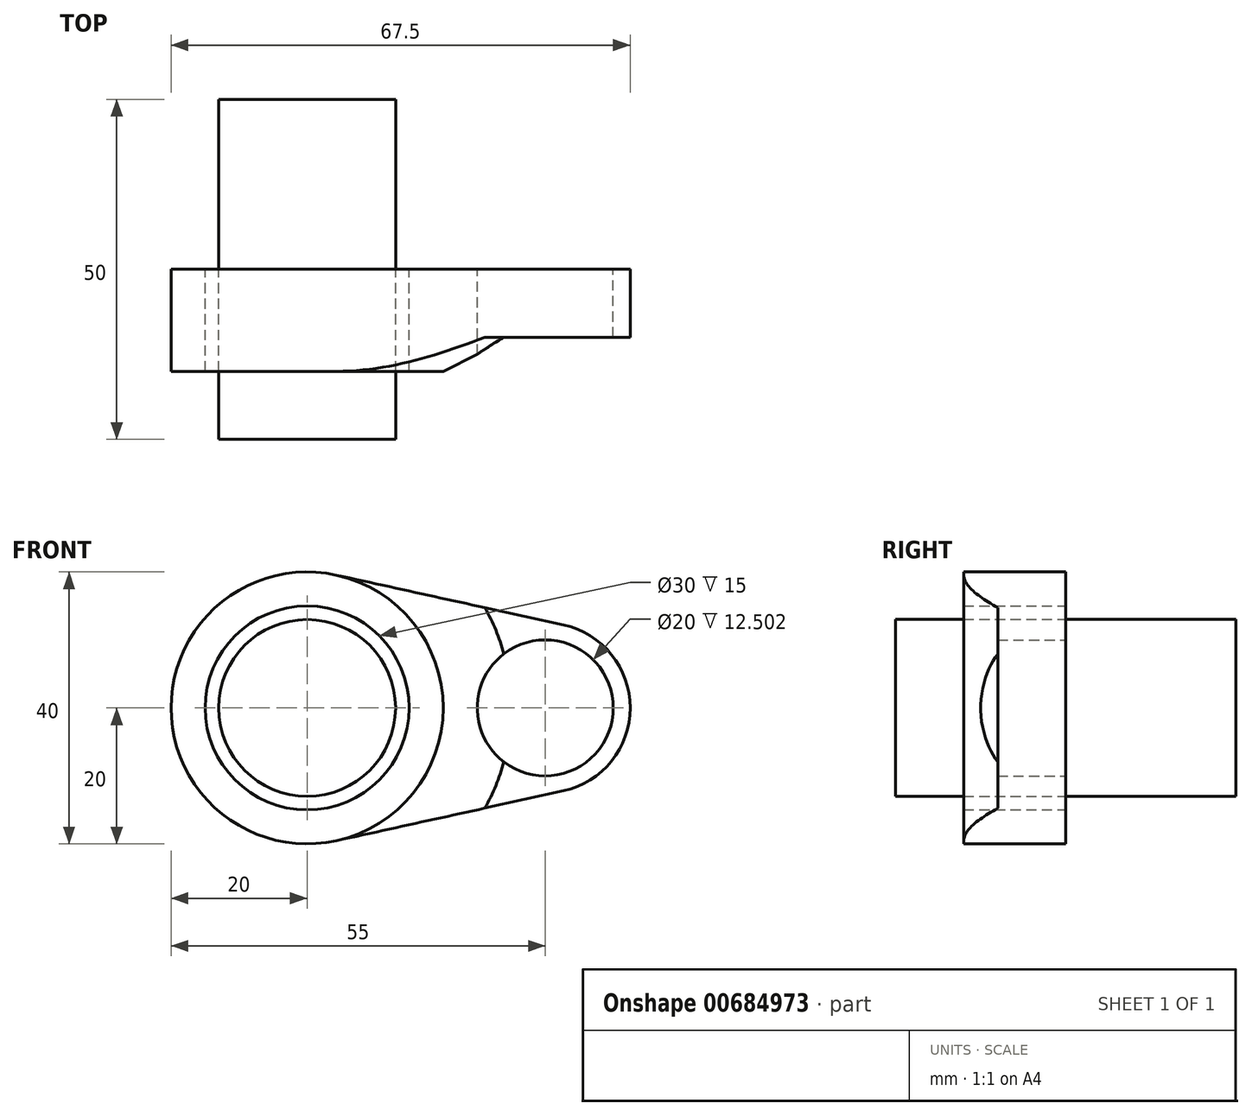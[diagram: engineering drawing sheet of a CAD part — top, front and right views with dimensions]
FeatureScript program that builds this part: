
annotation { "Feature Type Name" : "Feature", "Feature Type Description" : "" }
export const myFeature = defineFeature(function(context is Context, id is Id, definition is map)
    precondition{}
    {
        {
            var Q0;
            Q0=qCreatedBy(makeId("Front.planeOp"),FACE);
            var sketch = newSketch(context, id + "F0", { "sketchPlane" : qUnion([Q0])});
            skCircle(sketch, "E0", {"center": v(0, 0) * mm, "radius": 20 * mm});
            skCircle(sketch, "E1", {"center": v(35, 0) * mm, "radius": 12.5 * mm});
            skLineSegment(sketch, "E2", {"start": v(4.29, 19.54) * mm, "end": v(37.68, 12.2) * mm});
            skLineSegment(sketch, "E3", {"start": v(4.29, -19.54) * mm, "end": v(37.68, -12.2) * mm});
            skCircle(sketch, "E4", {"center": v(0, 0) * mm, "radius": 15 * mm});
            skCircle(sketch, "E5", {"center": v(35, 0) * mm, "radius": 10 * mm});
            skSolve(sketch);
        }
        {
            var Q0;
            Q0 = qSketchRegion(id + "F0", true);
            extrude(context, id + "F1", {"entities" : qUnion([Q0]), "depth" : 10 * mm, "offsetDistance" : 25 * mm});
        }
        {
            var Q0;
            Q0=makeQuery(id+"F0.imprint","IMPRINT",FACE,{"disambiguationData":[TD([[makeQuery(id+"F0.imprint","IMPRINT",EDGE,{"derivedFrom":sQuery(id+"F0.wireOp",EDGE,"E4")}),-1.0]])]});
            extrude(context, id + "F2", {"entities" : qUnion([Q0]), "operationType" : NewBodyOperationType.ADD, "depth" : 15 * mm, "offsetDistance" : 25 * mm});
        }
        {
            var Q0;
            {var subQ0=sQuery(id+"F0.wireOp",EDGE,"E0");Q0=makeQuery(id+"F2.boolean.opBoolean","INTERSECT",EDGE,{"derivedFrom":[makeQuery(id+"F1.opExtrude","CAP_FACE",FACE,{"disambiguationData":[OSD([subQ0,sQuery(id+"F0.wireOp",EDGE,"E1"),sQuery(id+"F0.wireOp",EDGE,"E2"),sQuery(id+"F0.wireOp",EDGE,"E3"),sQuery(id+"F0.wireOp",EDGE,"E4"),sQuery(id+"F0.wireOp",EDGE,"E5")])],"isStart":false}),makeQuery(id+"F2.opExtrude","SWEPT_FACE",FACE,{"disambiguationData":[OSD([subQ0])]})]});}
            chamfer(context, id + "F3", {"entities" : qUnion([Q0]), "chamferType" : ChamferType.TWO_OFFSETS, "width1" : 10 * mm, "oppositeDirection" : false, "width2" : 5 * mm, "tangentPropagation" : true});
        }
        {
            var Q0;
            Q0=qCreatedBy(makeId("Front.planeOp"),FACE);
            var sketch = newSketch(context, id + "F4", { "sketchPlane" : qUnion([Q0])});
            skCircle(sketch, "E6", {"center": v(0, 0) * mm, "radius": 13 * mm});
            skSolve(sketch);
        }
        {
            var Q0;
            Q0=makeQuery(id+"F4.imprint","IMPRINT",FACE,{"disambiguationData":[TD([[makeQuery(id+"F4.imprint","IMPRINT",EDGE,{"derivedFrom":sQuery(id+"F4.wireOp",EDGE,"E6")}),1.0]])]});
            var Q1;
            Q1=sQuery(id+"F0.wireOp",EDGE,"E4");
            extrude(context, id + "F5", {"entities" : qUnion([Q0]), "surfaceEntities" : qUnion([Q1]), "endBound" : BoundingType.SYMMETRIC, "depth" : 50 * mm, "offsetDistance" : 25 * mm});
        }
    });
